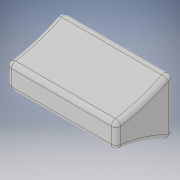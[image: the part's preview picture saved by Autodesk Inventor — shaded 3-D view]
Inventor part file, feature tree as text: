
AUTODESK INVENTOR PART (.ipt)
format: ipt  version: 2018.3 (Build 223284000, 284)  size: 188,416 bytes
history: native  units: mm
features: extrude x4, sketch x4, projected_geometry x3, fillet x2
ambient origin geometry x8: Origin, YZ Plane, XZ Plane, XY Plane, X Axis, Y Axis, Z Axis, Center Point
bodies: Body1 (feature_tree)
feature tree (13):
  extrude  "Extrusion5"  Depth=23.0mm
  extrude  "Extrusion6"  Depth=4.0mm
  extrude  "Extrusion7"  TaperAngle=0.0deg  [1 undecoded]
  extrude  "Extrusion8"  Depth=2.0mm
  fillet  "Fillet2"  Radius=11.5mm
  fillet  "Fillet3"  Radius=3.75mm
  sketch  "Sketch6"  dims[d29=23.0mm d30=13.0mm]
  sketch  "Sketch7"  dims[d31=12.0mm d32=0.0mm d33=4.0mm]
  projected_geometry  "Projected Loop2"
  sketch  "Sketch8"  dims[d34=4.0mm d37=0.0mm d38=0.0mm]
  sketch  "Sketch9"  dims[d39=2.0mm d40=2.0mm d41=11.5mm d42=3.75mm d43=5.0mm d44=5.0mm d45=8.0mm d46=0.0mm d47=0.2mm d48=0.2mm d49=2.0mm d50=0.0mm d51=4.0mm d52=4.0mm d53=1.0mm d54=1.0mm]
  projected_geometry  "Projected Loop3"
  projected_geometry  "Projected Loop4"
note: 1 required parameter value undecoded (feature->parameter linkage not recoverable at this tier; creation-order binding heuristic only, values carry confidence <= 0.55)
